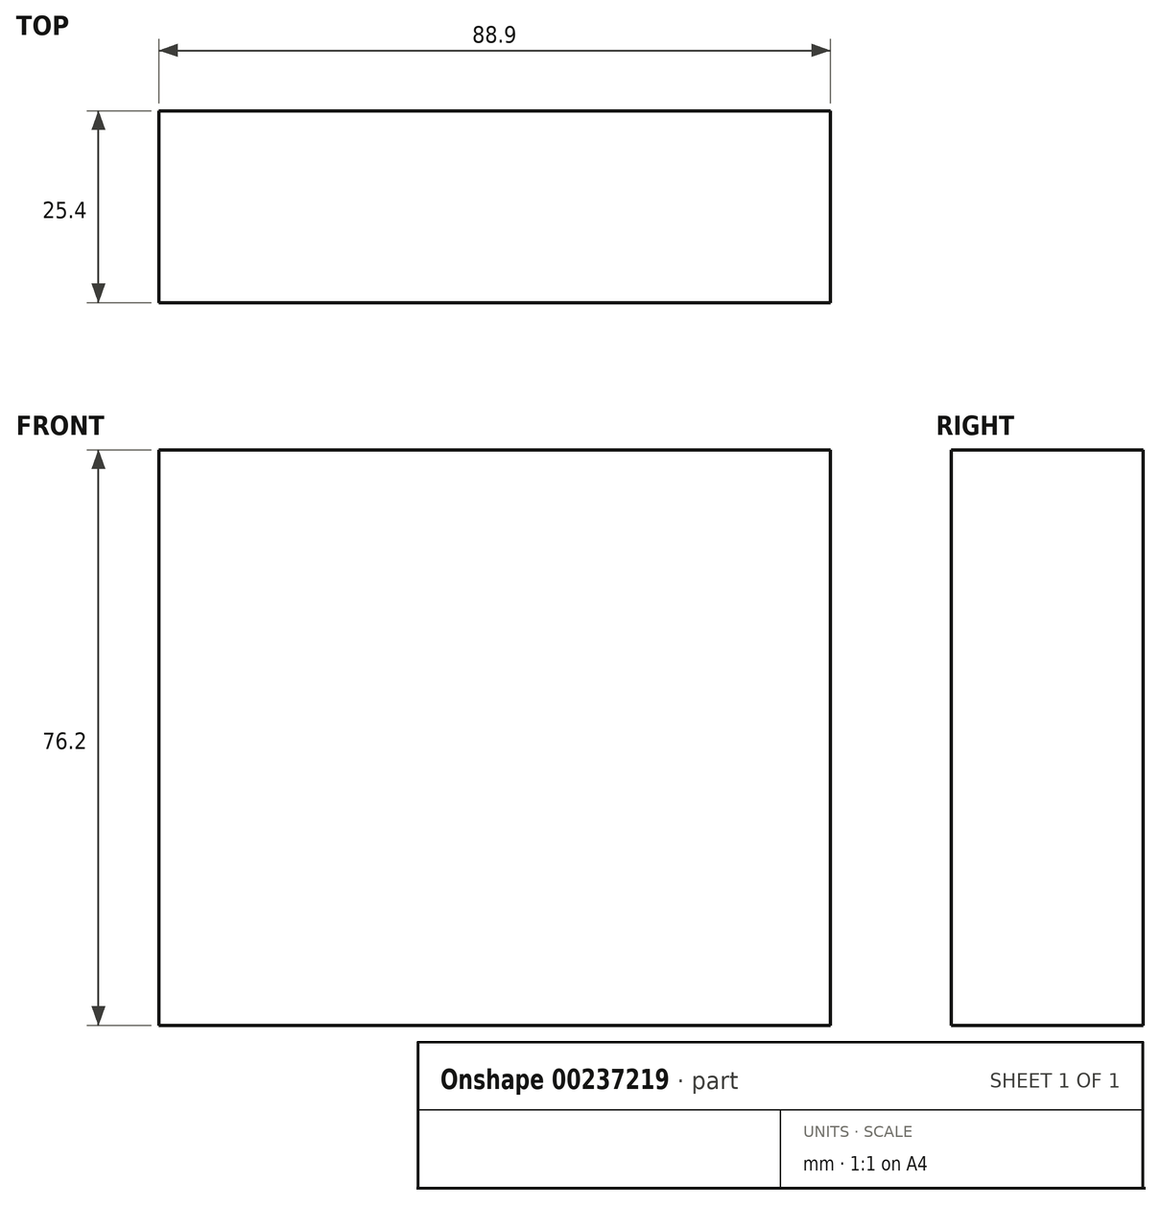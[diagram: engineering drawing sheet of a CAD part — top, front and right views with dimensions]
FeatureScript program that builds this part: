
annotation { "Feature Type Name" : "Feature", "Feature Type Description" : "" }
export const myFeature = defineFeature(function(context is Context, id is Id, definition is map)
    precondition{}
    {
        {
            var Q0;
            Q0=qCreatedBy(makeId("Top.planeOp"),FACE);
            var sketch = newSketch(context, id + "F0", { "sketchPlane" : qUnion([Q0])});
            skLineSegment(sketch, "E0.bottom", {"start": v(57.14, 13.95) * mm, "end": v(-31.76, 13.95) * mm});
            skLineSegment(sketch, "E0.top", {"start": v(57.14, -11.45) * mm, "end": v(-31.76, -11.45) * mm});
            skLineSegment(sketch, "E0.left", {"start": v(57.14, 13.95) * mm, "end": v(57.14, -11.45) * mm});
            skLineSegment(sketch, "E0.right", {"start": v(-31.76, 13.95) * mm, "end": v(-31.76, -11.45) * mm});
            skSolve(sketch);
        }
        {
            var Q0;
            Q0 = qSketchRegion(id + "F0", true);
            extrude(context, id + "F1", {"entities" : qUnion([Q0]), "depth" : 76.2 * mm});
        }
    });
